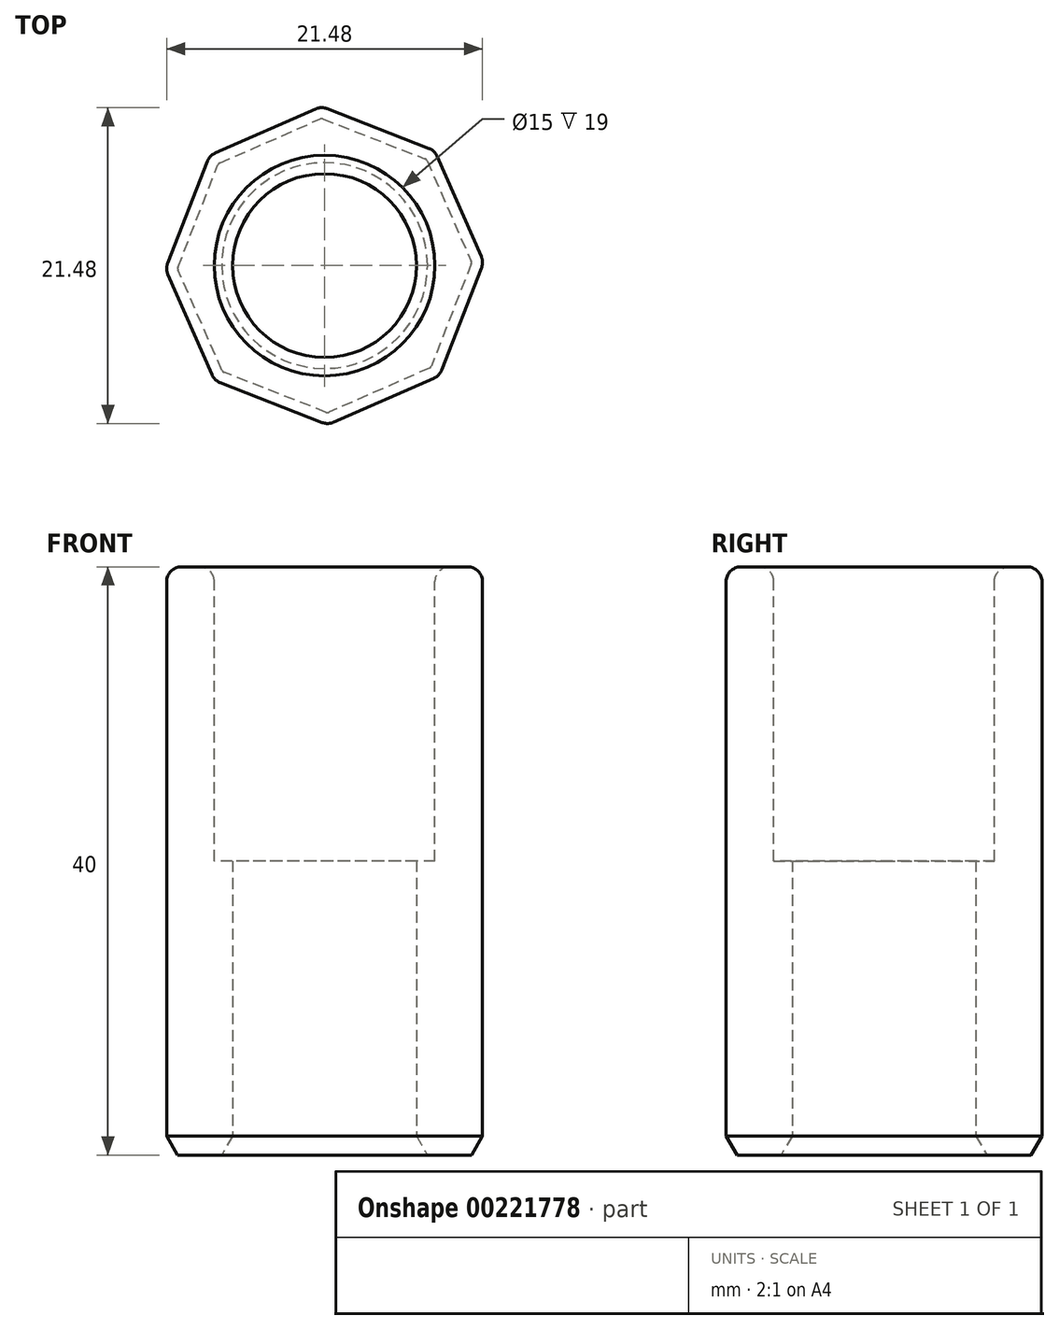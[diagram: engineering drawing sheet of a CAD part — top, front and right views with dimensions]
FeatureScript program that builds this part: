
annotation { "Feature Type Name" : "Feature", "Feature Type Description" : "" }
export const myFeature = defineFeature(function(context is Context, id is Id, definition is map)
    precondition{}
    {
        {
            var Q0;
            Q0=qCreatedBy(makeId("Top.planeOp"),FACE);
            var sketch = newSketch(context, id + "F0", { "sketchPlane" : qUnion([Q0])});
            skCircle(sketch, "E0", {"center": v(0, 0) * mm, "radius": 6.25 * mm});
            skCircle(sketch, "E1.cCircle", {"center": v(0, 0) * mm, "radius": 10 * mm, "construction": true});
            skLineSegment(sketch, "E1.0", {"start": v(-7.81, 7.5) * mm, "end": v(-0.22, 10.82) * mm});
            skLineSegment(sketch, "E1.1", {"start": v(-0.22, 10.82) * mm, "end": v(7.5, 7.81) * mm});
            skLineSegment(sketch, "E1.2", {"start": v(7.5, 7.81) * mm, "end": v(10.82, 0.22) * mm});
            skLineSegment(sketch, "E1.3", {"start": v(10.82, 0.22) * mm, "end": v(7.81, -7.5) * mm});
            skLineSegment(sketch, "E1.4", {"start": v(7.81, -7.5) * mm, "end": v(0.22, -10.82) * mm});
            skLineSegment(sketch, "E1.5", {"start": v(0.22, -10.82) * mm, "end": v(-7.5, -7.81) * mm});
            skLineSegment(sketch, "E1.6", {"start": v(-7.5, -7.81) * mm, "end": v(-10.82, -0.22) * mm});
            skLineSegment(sketch, "E1.7", {"start": v(-10.82, -0.22) * mm, "end": v(-7.81, 7.5) * mm});
            skPoint(sketch, "E1.0.midPoint", {"position": v(-4.02, 9.16) * mm});
            skSolve(sketch);
        }
        {
            var Q0;
            Q0 = qSketchRegion(id + "F0", true);
            extrude(context, id + "F1", {"entities" : qUnion([Q0]), "depth" : 40 * mm});
        }
        {
            var Q0;
            Q0=makeQuery(id+"F1.opExtrude","CAP_FACE",FACE,{"disambiguationData":[OSD([sQuery(id+"F0.wireOp",EDGE,"E0"),sQuery(id+"F0.wireOp",EDGE,"E1.0"),sQuery(id+"F0.wireOp",EDGE,"E1.1"),sQuery(id+"F0.wireOp",EDGE,"E1.2"),sQuery(id+"F0.wireOp",EDGE,"E1.3"),sQuery(id+"F0.wireOp",EDGE,"E1.4"),sQuery(id+"F0.wireOp",EDGE,"E1.5"),sQuery(id+"F0.wireOp",EDGE,"E1.6"),sQuery(id+"F0.wireOp",EDGE,"E1.7")])],"isStart":false});
            var sketch = newSketch(context, id + "F2", { "sketchPlane" : qUnion([Q0])});
            skCircle(sketch, "E2", {"center": v(0, 0) * mm, "radius": 7.5 * mm});
            skSolve(sketch);
        }
        {
            var Q0;
            Q0 = qSketchRegion(id + "F2", true);
            extrude(context, id + "F3", {"entities" : qUnion([Q0]), "operationType" : NewBodyOperationType.REMOVE, "oppositeDirection" : true, "depth" : 20 * mm});
        }
        {
            var Q0;
            Q0=makeQuery(id+"F1.opExtrude","SWEPT_EDGE",EDGE,{"disambiguationData":[OSD([sQuery(id+"F0.wireOp",EDGE,"E1.6"),sQuery(id+"F0.wireOp",EDGE,"E1.7")])]});
            var Q1;
            Q1=makeQuery(id+"F1.opExtrude","SWEPT_EDGE",EDGE,{"disambiguationData":[OSD([sQuery(id+"F0.wireOp",EDGE,"E1.5"),sQuery(id+"F0.wireOp",EDGE,"E1.6")])]});
            var Q2;
            Q2=makeQuery(id+"F1.opExtrude","SWEPT_EDGE",EDGE,{"disambiguationData":[OSD([sQuery(id+"F0.wireOp",EDGE,"E1.4"),sQuery(id+"F0.wireOp",EDGE,"E1.5")])]});
            var Q3;
            Q3=makeQuery(id+"F1.opExtrude","SWEPT_EDGE",EDGE,{"disambiguationData":[OSD([sQuery(id+"F0.wireOp",EDGE,"E1.3"),sQuery(id+"F0.wireOp",EDGE,"E1.4")])]});
            var Q4;
            Q4=makeQuery(id+"F1.opExtrude","SWEPT_EDGE",EDGE,{"disambiguationData":[OSD([sQuery(id+"F0.wireOp",EDGE,"E1.2"),sQuery(id+"F0.wireOp",EDGE,"E1.3")])]});
            var Q5;
            Q5=makeQuery(id+"F1.opExtrude","SWEPT_EDGE",EDGE,{"disambiguationData":[OSD([sQuery(id+"F0.wireOp",EDGE,"E1.1"),sQuery(id+"F0.wireOp",EDGE,"E1.2")])]});
            var Q6;
            Q6=makeQuery(id+"F1.opExtrude","SWEPT_EDGE",EDGE,{"disambiguationData":[OSD([sQuery(id+"F0.wireOp",EDGE,"E1.0"),sQuery(id+"F0.wireOp",EDGE,"E1.1")])]});
            var Q7;
            Q7=makeQuery(id+"F1.opExtrude","SWEPT_EDGE",EDGE,{"disambiguationData":[OSD([sQuery(id+"F0.wireOp",EDGE,"E1.0"),sQuery(id+"F0.wireOp",EDGE,"E1.7")])]});
            fillet(context, id + "F4", {"entities" : qUnion([Q0, Q1, Q2, Q3, Q4, Q5, Q6, Q7]), "radius" : 1 * mm, "tangentPropagation" : true, "allowEdgeOverflow" : false});
        }
        {
            var Q0;
            Q0=makeQuery(id+"F1.opExtrude","CAP_FACE",FACE,{"disambiguationData":[OSD([sQuery(id+"F0.wireOp",EDGE,"E0"),sQuery(id+"F0.wireOp",EDGE,"E1.0"),sQuery(id+"F0.wireOp",EDGE,"E1.1"),sQuery(id+"F0.wireOp",EDGE,"E1.2"),sQuery(id+"F0.wireOp",EDGE,"E1.3"),sQuery(id+"F0.wireOp",EDGE,"E1.4"),sQuery(id+"F0.wireOp",EDGE,"E1.5"),sQuery(id+"F0.wireOp",EDGE,"E1.6"),sQuery(id+"F0.wireOp",EDGE,"E1.7")])],"isStart":true});
            chamfer(context, id + "F5", {"entities" : qUnion([Q0]), "chamferType" : ChamferType.OFFSET_ANGLE, "width" : .75 * mm, "oppositeDirection" : false, "angle" : 60 * degree, "tangentPropagation" : true});
        }
        {
            var Q0;
            Q0=makeQuery(id+"F1.opExtrude","CAP_FACE",FACE,{"disambiguationData":[OSD([sQuery(id+"F0.wireOp",EDGE,"E0"),sQuery(id+"F0.wireOp",EDGE,"E1.0"),sQuery(id+"F0.wireOp",EDGE,"E1.1"),sQuery(id+"F0.wireOp",EDGE,"E1.2"),sQuery(id+"F0.wireOp",EDGE,"E1.3"),sQuery(id+"F0.wireOp",EDGE,"E1.4"),sQuery(id+"F0.wireOp",EDGE,"E1.5"),sQuery(id+"F0.wireOp",EDGE,"E1.6"),sQuery(id+"F0.wireOp",EDGE,"E1.7")])],"isStart":false});
            fillet(context, id + "F6", {"entities" : qUnion([Q0]), "radius" : 1 * mm, "tangentPropagation" : true, "allowEdgeOverflow" : false});
        }
    });
